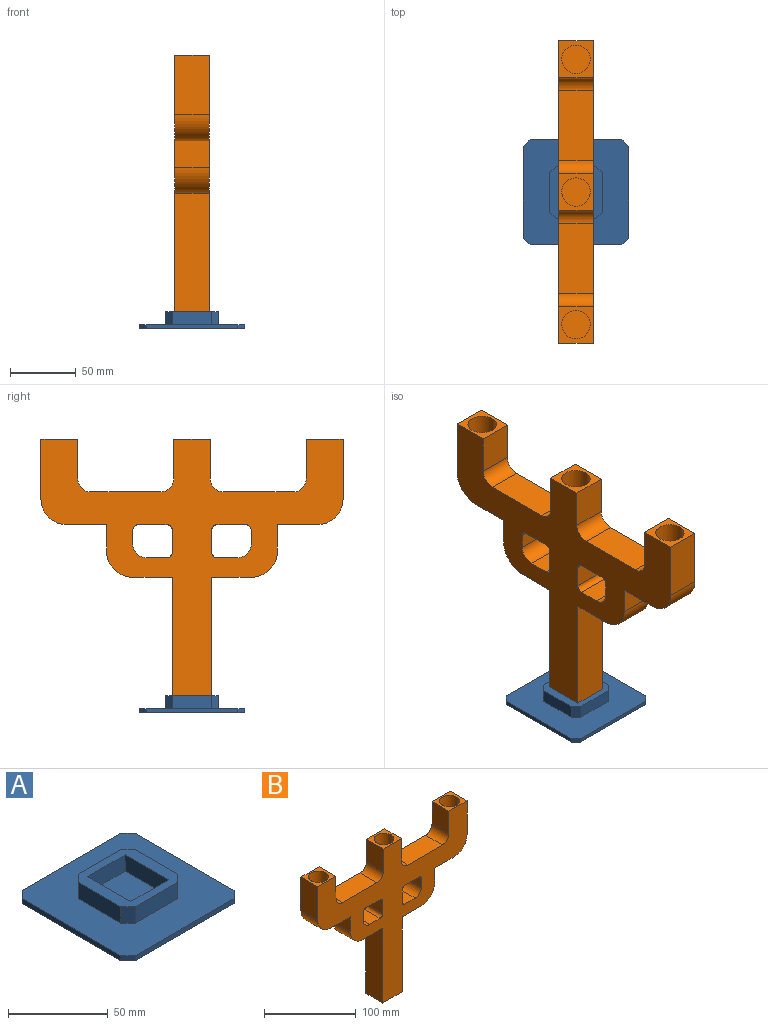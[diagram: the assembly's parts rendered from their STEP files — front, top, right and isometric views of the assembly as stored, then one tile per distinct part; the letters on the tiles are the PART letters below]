
ASSEMBLY  parts=2 mates=1
PART A: 24 faces, bbox 80x80x13 mm
  f0: plane 40x40mm, normal (0,0,1), area 736mm2, adj f7,f8,f9,f10,f11,f12,f13,f14
  f1: plane 80x80mm, normal (0,0,1), area 4800mm2, adj f2,f3,f4,f5,f7,f8,f9,f10
  f2: plane 70x3mm, normal (0,1,0), area 210mm2, adj f1,f6,f20,f21
  f3: plane 70x3mm, normal (-1,0,0), area 210mm2, adj f1,f6,f20,f22
  f4: plane 70x3mm, normal (0,-1,0), area 210mm2, adj f1,f6,f22,f23
  f5: plane 70x3mm, normal (1,0,0), area 210mm2, adj f1,f6,f21,f23
  f6: plane 80x80mm, normal (0,0,-1), area 6350mm2, adj f2,f3,f4,f5,f20,f21,f22,f23
  f7: plane 30x10mm, normal (0,1,0), area 300mm2, adj f0,f1,f18,f19
  f8: plane 30x10mm, normal (-1,0,0), area 300mm2, adj f0,f1,f16,f19
  f9: plane 30x10mm, normal (0,-1,0), area 300mm2, adj f0,f1,f16,f17
  f10: plane 30x10mm, normal (1,0,0), area 300mm2, adj f0,f1,f17,f18
  f11: plane 26.6x10mm, normal (0,-1,0), area 266mm2, adj f0,f12,f14,f15
  f12: plane 30.6x10mm, normal (1,0,0), area 306mm2, adj f0,f11,f13,f15
  f13: plane 26.6x10mm, normal (0,1,0), area 266mm2, adj f0,f12,f14,f15
  f14: plane 30.6x10mm, normal (-1,0,0), area 306mm2, adj f0,f11,f13,f15
  f15: plane 30.6x26.6mm, normal (0,0,1), area 814mm2, adj f11,f12,f13,f14
  f16: plane 10x5mm, normal (-0.71,-0.71,0), area 70.7mm2, adj f0,f1,f8,f9
  f17: plane 10x5mm, normal (0.71,-0.71,0), area 70.7mm2, adj f0,f1,f9,f10
  f18: plane 10x5mm, normal (0.71,0.71,0), area 70.7mm2, adj f0,f1,f7,f10
  f19: plane 10x5mm, normal (-0.71,0.71,0), area 70.7mm2, adj f0,f1,f7,f8
  f20: plane 5x5mm, normal (-0.71,0.71,0), area 21.2mm2, adj f1,f2,f3,f6
  f21: plane 5x5mm, normal (0.71,0.71,0), area 21.2mm2, adj f1,f2,f5,f6
  f22: plane 5x5mm, normal (-0.71,-0.71,0), area 21.2mm2, adj f1,f3,f4,f6
  f23: plane 5x5mm, normal (0.71,-0.71,0), area 21.2mm2, adj f1,f4,f5,f6
PART B: 52 faces, bbox 230x26x205 mm
  f0: plane 26x17mm, normal (1,0,0), area 442mm2, adj f28,f29,f49,f51
  f1: plane 26x22mm, normal (0,0,-1), area 572mm2, adj f28,f29,f49,f50
  f2: plane 26x11mm, normal (-1,0,0), area 286mm2, adj f28,f29,f35,f50
  f3: plane 53x26mm, normal (0,0,1), area 1378mm2, adj f28,f29,f31,f34
  f4: plane 30x26mm, normal (1,0,0), area 780mm2, adj f5,f28,f29,f31
  f5: plane 28x26mm, normal (0,0,1), area 361.6mm2, adj f4,f6,f28,f29,f40
  f6: plane 30x26mm, normal (-1,0,0), area 780mm2, adj f5,f28,f29,f32
  f7: plane 53x26mm, normal (0,0,1), area 1378mm2, adj f28,f29,f32,f33
  f8: plane 30x26mm, normal (1,0,0), area 780mm2, adj f9,f28,f29,f33
  f9: plane 28x26mm, normal (0,0,1), area 361.6mm2, adj f8,f10,f28,f29,f38
  f10: plane 45x26mm, normal (-1,0,0), area 1170mm2, adj f9,f28,f29,f44
  f11: plane 30x26mm, normal (0,0,-1), area 780mm2, adj f12,f28,f29,f44
  f12: plane 26x20mm, normal (-1,0,0), area 520mm2, adj f11,f28,f29,f36
  f13: plane 30x26mm, normal (0,0,-1), area 780mm2, adj f14,f28,f29,f36
  f14: plane 100x26mm, normal (-1,0,0), area 2600mm2, adj f13,f15,f28,f29
  f15: plane 30x26mm, normal (0,0,-1), area 780mm2, adj f14,f16,f28,f29
  f16: plane 100x26mm, normal (1,0,0), area 2600mm2, adj f15,f17,f28,f29
  f17: plane 30x26mm, normal (0,0,-1), area 780mm2, adj f16,f28,f29,f37
  f18: plane 26x20mm, normal (1,0,0), area 520mm2, adj f19,f28,f29,f37
  f19: plane 30x26mm, normal (0,0,-1), area 780mm2, adj f18,f28,f29,f45
  f20: plane 45x26mm, normal (1,0,0), area 1170mm2, adj f21,f28,f29,f45
  f21: plane 28x26mm, normal (0,0,1), area 361.6mm2, adj f20,f25,f28,f29,f42
  f22: plane 26x17mm, normal (-1,0,0), area 442mm2, adj f28,f29,f46,f48
  f23: plane 26x16mm, normal (0,0,1), area 416mm2, adj f28,f29,f30,f46
  f24: plane 26x11mm, normal (1,0,0), area 286mm2, adj f28,f29,f30,f47
  f25: plane 30x26mm, normal (-1,0,0), area 780mm2, adj f21,f28,f29,f34
  f26: plane 26x22mm, normal (0,0,-1), area 572mm2, adj f28,f29,f47,f48
  f27: plane 26x16mm, normal (0,0,1), area 416mm2, adj f28,f29,f35,f51
  f28: plane 230x205mm, normal (0,-1,0), area 15616mm2, adj f0,f1,f2,f3,f4,f5,f6,f7
  f29: plane 230x205mm, normal (0,1,0), area 15616mm2, adj f0,f1,f2,f3,f4,f5,f6,f7
  f30: cylinder r=10mm len=26mm, axis (0,-1,0), area 408.4mm2, adj f23,f24,f28,f29
  f31: cylinder r=10mm len=26mm, axis (0,1,0), area 408.4mm2, adj f3,f4,f28,f29
  f32: cylinder r=10mm len=26mm, axis (0,1,0), area 408.4mm2, adj f6,f7,f28,f29
  f33: cylinder r=10mm len=26mm, axis (0,-1,0), area 408.4mm2, adj f7,f8,f28,f29
  f34: cylinder r=10mm len=26mm, axis (0,-1,0), area 408.4mm2, adj f3,f25,f28,f29
  f35: cylinder r=10mm len=26mm, axis (0,-1,0), area 408.4mm2, adj f2,f27,f28,f29
  f36: cylinder r=20mm len=26mm, axis (0,1,0), area 816.8mm2, adj f12,f13,f28,f29
  f37: cylinder r=20mm len=26mm, axis (0,1,0), area 816.8mm2, adj f17,f18,f28,f29
  f38: cylinder r=10.8mm len=25mm, axis (0,0,1), area 1696.5mm2, adj f9,f39
  f39: plane 21.6x21.6mm, normal (0,0,1), area 366.4mm2, adj f38
  f40: cylinder r=10.8mm len=25mm, axis (0,0,1), area 1696.5mm2, adj f5,f41
  f41: plane 21.6x21.6mm, normal (0,0,1), area 366.4mm2, adj f40
  f42: cylinder r=10.8mm len=25mm, axis (0,0,1), area 1696.5mm2, adj f21,f43
  f43: plane 21.6x21.6mm, normal (0,0,1), area 366.4mm2, adj f42
  f44: cylinder r=20mm len=26mm, axis (0,-1,0), area 816.8mm2, adj f10,f11,f28,f29
  f45: cylinder r=20mm len=26mm, axis (0,-1,0), area 816.8mm2, adj f19,f20,f28,f29
  f46: cylinder r=4mm len=26mm, axis (0,-1,0), area 163.4mm2, adj f22,f23,f28,f29
  f47: cylinder r=4mm len=26mm, axis (0,-1,0), area 163.4mm2, adj f24,f26,f28,f29
  f48: cylinder r=4mm len=26mm, axis (0,-1,0), area 163.4mm2, adj f22,f26,f28,f29
  f49: cylinder r=4mm len=26mm, axis (0,-1,0), area 163.4mm2, adj f0,f1,f28,f29
  f50: cylinder r=4mm len=26mm, axis (0,-1,0), area 163.4mm2, adj f1,f2,f28,f29
  f51: cylinder r=4mm len=26mm, axis (0,-1,0), area 163.4mm2, adj f0,f27,f28,f29
PLACE A t=(-138.54,-14.01,-120.25)mm
PLACE B rot(axis=(0,0,-1),90deg) t=(-85.54,-54.01,-117.25)mm
MATE fastened B.f40 <-> A.f15  axis (0,0,-1) through (-98.54,-54.01,-117.25)mm
